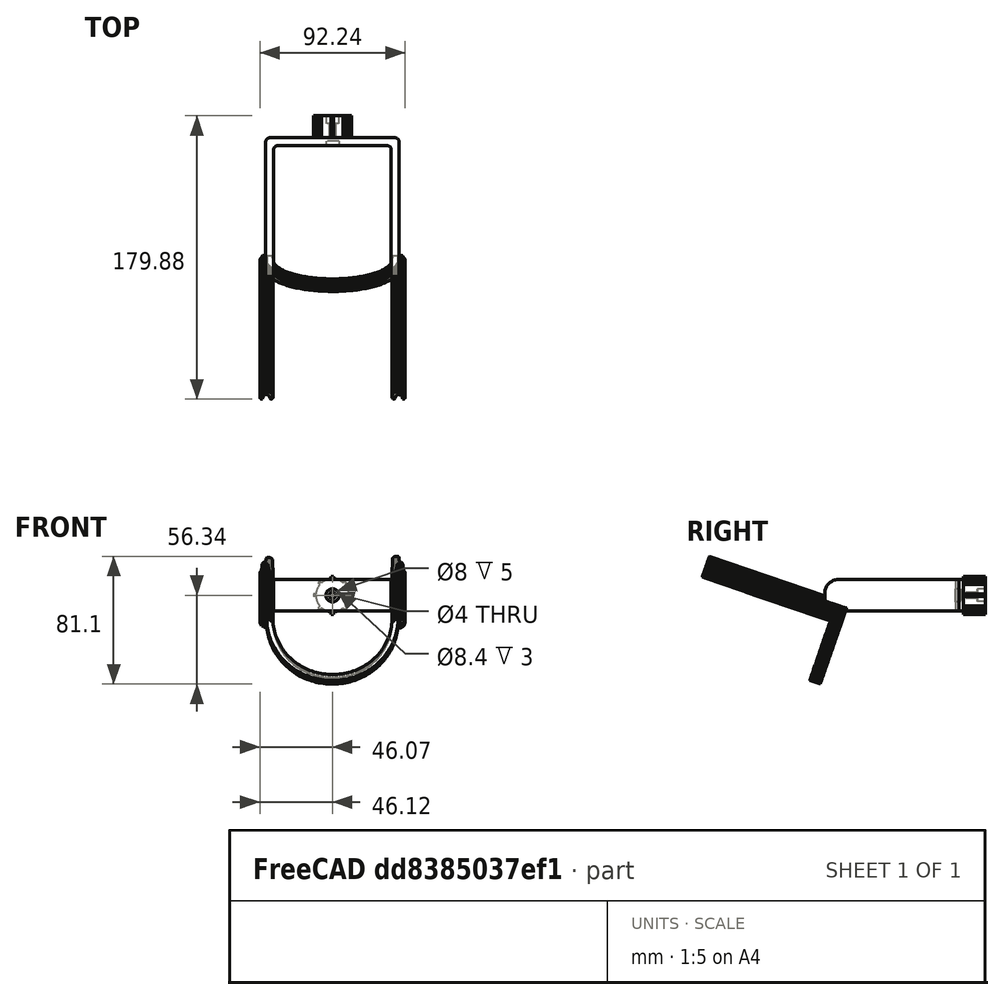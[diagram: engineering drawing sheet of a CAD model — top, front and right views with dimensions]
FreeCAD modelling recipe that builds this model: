
FCSTD DOCUMENT  (FreeCAD 0.18R4 (GitTag))
Label: 01_bracket
License: All rights reserved
LicenseURL: http://en.wikipedia.org/wiki/All_rights_reserved
objects: Part::Box×9, Part::Cut×7, Part::Cylinder×6, Part::MultiFuse×5, Part::Fillet×2, Part::MultiCommon×2, Part::Feature×1, Part::FeaturePython×1, Mesh::Feature×1
note: 33 computed .brp shape members not serialized (recipe doc carries the construction recipe); baked Part::Feature solids carry a one-line shape summary decoded from their .brp

FEATURE [Part::Feature] _1_bracket001001_solid  label="_1_bracket002 (Solid)"
  Placement = pos=(0,-184.21,-18.54) rot=(0.631347,-0.631347,-0.450335;3.9879rad)
  shape: bbox 92.24 x 94.45 x 81.1 mm, 2613 faces (baked)
FEATURE [Part::Cylinder] Cylinder059  label="Cylinder054"
  Angle = 360
  AttacherType = Attacher::AttachEngine3D
  Height = 2.6
  Placement = pos=(0,0,1) rot=(0,0,1;0rad)
  Radius = 3.25
FEATURE [Part::Cylinder] Cylinder057  label="Cylinder052"
  Angle = 360
  AttacherType = Attacher::AttachEngine3D
  Height = 13
  Placement = pos=(0,0,3.6) rot=(0,0,1;0rad)
  Radius = 2
FEATURE [Part::Cylinder] Cylinder055  label="base_para_rosca_microfono"
  Angle = 360
  AttacherType = Attacher::AttachEngine3D
  Height = 14
  Radius = 10.5
FEATURE [Part::Box] Box019  label="Cube019"
  AttacherType = Attacher::AttachEngine3D
  Height = 14
  Length = 6
  Placement = pos=(6,-0.75,0) rot=(0,0,1;0rad)
  Width = 1.5
FEATURE [Part::FeaturePython] Array004  # Draft array (typed FeaturePython)
  Angle = 360
  ArrayType = 1
  Axis = (0,0,1)
  Base = -> Box019
  Center = (0,0,0)
  Fuse = false
  IntervalAxis = (0,0,0)
  IntervalX = (1,0,0)
  IntervalY = (0,1,0)
  IntervalZ = (0,0,1)
  NumberPolar = 8
  NumberX = 2
  NumberY = 2
  NumberZ = 1
FEATURE [Part::MultiFuse] Fusion021  label="base_para_rosca_microfono001"
  Placement = pos=(0,0,1) rot=(0,0,1;0rad)
  Shapes = -> [Cylinder055,Array004]
FEATURE [Part::Cut] Cut043
  Base = -> Fusion021
  Refine = true
  Tool = -> Cylinder059
FEATURE [Part::Cut] Cut044  label="base_para_rosca_microfono_final"
  Base = -> Cut043
  Placement = pos=(-0.05,-83,-22) rot=(1,0,0;1.5708rad)
  Refine = true
  Tool = -> Cylinder057
FEATURE [Part::Cylinder] Cylinder
  Angle = 360
  AttacherType = Attacher::AttachEngine3D
  Height = 14
  Placement = pos=(0,-88,-22) rot=(1,0,0;1.5708rad)
  Radius = 2
FEATURE [Part::Cylinder] Cylinder060  label="Cylinder055"
  Angle = 360
  AttacherType = Attacher::AttachEngine3D
  Height = 10
  Placement = pos=(0,-78,-22) rot=(1,0,0;1.5708rad)
  Radius = 4
FEATURE [Part::MultiFuse] Fusion  label="corta_tonillo"
  Placement = pos=(-0.05,-1,0) rot=(0,0,1;0rad)
  Refine = true
  Shapes = -> [Cylinder,Cylinder060]
FEATURE [Part::Box] Box  label="Cube"
  AttacherType = Attacher::AttachEngine3D
  Height = 20
  Length = 84.6
  Placement = pos=(-42.4,-103,-32) rot=(0,0,1;0rad)
  Width = 5
FEATURE [Part::Box] Box020  label="Cube020"
  AttacherType = Attacher::AttachEngine3D
  Height = 20
  Length = 5
  Placement = pos=(37.3,-186,-32) rot=(0,0,1;0rad)
  Width = 85
FEATURE [Part::Box] Box021  label="Cube021"
  AttacherType = Attacher::AttachEngine3D
  Height = 20
  Length = 5
  Placement = pos=(-42.4,-186,-32) rot=(0,0,1;0rad)
  Width = 85
FEATURE [Part::MultiFuse] Fusion022
  Refine = true
  Shapes = -> [Box,Box021,Box020]
FEATURE [Part::MultiFuse] Fusion023
  Refine = true
  Shapes = -> [_1_bracket001001_solid,Fusion022]
FEATURE [Part::Fillet] Fillet
  Base = -> Fusion023
  Edges = 2 edges r=8.5: [Edge1928,Edge1930]
FEATURE [Part::Fillet] Fillet001
  Base = -> Fillet
  Edges = 4 edges r=2.5: [Edge492,Edge607,Edge614,Edge615]
FEATURE [Part::Box] Box022  label="Cube022"
  AttacherType = Attacher::AttachEngine3D
  Height = 28
  Length = 10
  Placement = pos=(42.3,-184,-25) rot=(0,0,1;0rad)
  Width = 79
FEATURE [Part::Cut] Cut
  Base = -> Fillet001
  Refine = true
  Tool = -> Box022
FEATURE [Part::MultiFuse] Fusion024
  Refine = true
  Shapes = -> [Cut044,Cut]
FEATURE [Part::Cut] Cut045  label="_1_bracket"
  Base = -> Fusion024
  Refine = true
  Tool = -> Fusion
FEATURE [Part::Box] Box023  label="Cube023"
  AttacherType = Attacher::AttachEngine3D
  Height = 10
  Length = 3
  Placement = pos=(-40.4,-186,-32) rot=(0,0,1;0rad)
  Width = 8
FEATURE [Part::Box] Box024  label="Cube024"
  AttacherType = Attacher::AttachEngine3D
  Height = 20
  Length = 5
  Placement = pos=(-42.4,-186,-32) rot=(0,0,1;0rad)
  Width = 85
FEATURE [Part::MultiCommon] Common
  Placement = pos=(-2.3,-2.4,-5) rot=(0,0,1;0rad)
  Refine = true
  Shapes = -> [Box024,Box023]
FEATURE [Part::Box] Box025  label="Cube025"
  AttacherType = Attacher::AttachEngine3D
  Height = 20
  Length = 5
  Placement = pos=(37.3,-186,-32) rot=(0,0,1;0rad)
  Width = 85
FEATURE [Part::Box] Box026  label="Cube026"
  AttacherType = Attacher::AttachEngine3D
  Height = 10
  Length = 3
  Placement = pos=(37.3,-186,-32) rot=(0,0,1;0rad)
  Width = 8
FEATURE [Part::MultiCommon] Common001
  Placement = pos=(2,-3.1,-5) rot=(0,0,1;0rad)
  Refine = true
  Shapes = -> [Box025,Box026]
FEATURE [Part::Cut] Cut046
  Base = -> Cut045
  Refine = true
  Tool = -> Common
FEATURE [Part::Cut] Cut047  label="01-bracket_con_agujeros"
  Base = -> Cut046
  Refine = true
  Tool = -> Common001
FEATURE [Part::Cylinder] Cylinder061  label="Cylinder056"
  Angle = 360
  AttacherType = Attacher::AttachEngine3D
  Height = 10
  Placement = pos=(0,-100,-22) rot=(1,0,0;1.5708rad)
  Radius = 4.2
FEATURE [Part::Cut] Cut048  label="01-bracket_2"
  Base = -> Cut047
  Refine = true
  Tool = -> Cylinder061
FEATURE [Mesh::Feature] Mesh  label="01-bracket_2 (Meshed)"
